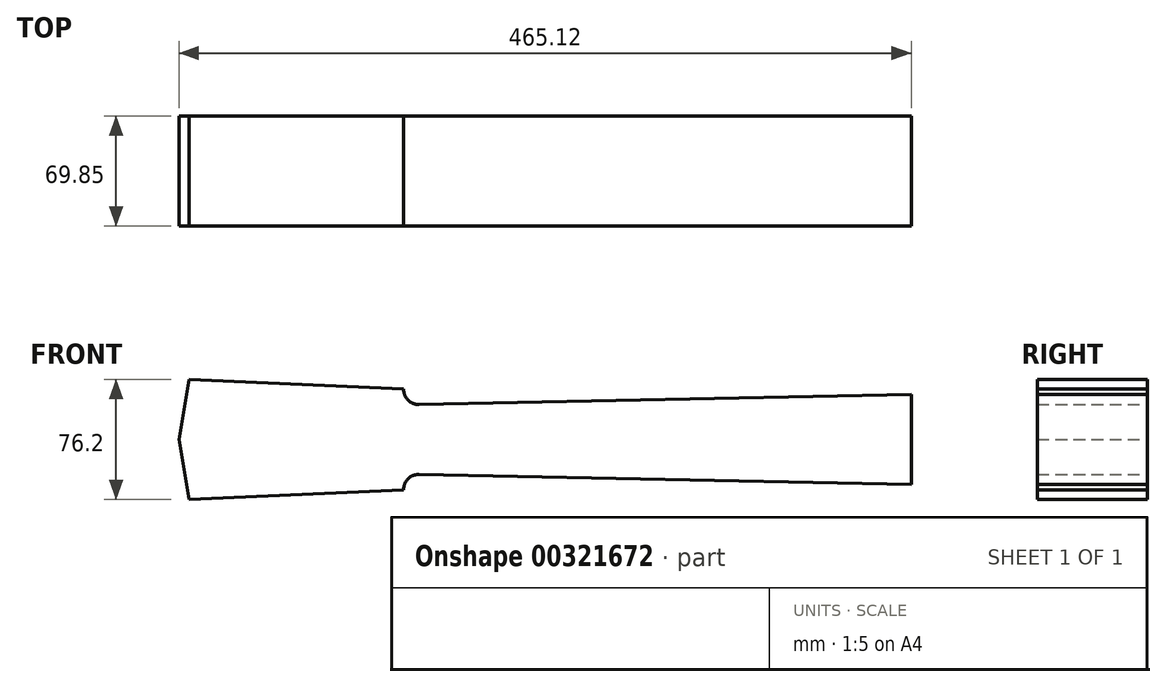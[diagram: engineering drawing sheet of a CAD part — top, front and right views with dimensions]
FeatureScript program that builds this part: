
annotation { "Feature Type Name" : "Feature", "Feature Type Description" : "" }
export const myFeature = defineFeature(function(context is Context, id is Id, definition is map)
    precondition{}
    {
        {
            var Q0;
            Q0=qCreatedBy(makeId("Front.planeOp"),FACE);
            var sketch = newSketch(context, id + "F0", { "sketchPlane" : qUnion([Q0])});
            skLineSegment(sketch, "E0", {"start": v(0, -28.57) * mm, "end": v(0, 28.57) * mm});
            skLineSegment(sketch, "E1", {"start": v(0, 28.58) * mm, "end": v(-312.72, 22.22) * mm});
            skLineSegment(sketch, "E2", {"start": v(-322.44, 32.16) * mm, "end": v(-458.77, 38.1) * mm});
            skLineSegment(sketch, "E3", {"start": v(-458.77, 38.1) * mm, "end": v(-465.12, 0) * mm});
            skLineSegment(sketch, "E4", {"start": v(-465.12, 0) * mm, "end": v(-458.77, -38.1) * mm});
            skLineSegment(sketch, "E5", {"start": v(-458.77, -38.1) * mm, "end": v(-322.44, -32.17) * mm});
            skLineSegment(sketch, "E6", {"start": v(-312.72, -22.23) * mm, "end": v(0, -28.58) * mm});
            skArc(sketch, "E7", {"start": v(-322.44, 32.16) * mm, "mid": v(-319.73, 25.1) * mm, "end": v(-312.72, 22.23) * mm});
            skArc(sketch, "E8", {"start": v(-312.72, -22.23) * mm, "mid": v(-319.74, -25.1) * mm, "end": v(-322.44, -32.17) * mm});
            skPoint(sketch, "E9.orphan", {"position": v(-312.72, -31.75) * mm});
            skSolve(sketch);
        }
        {
            var Q0;
            Q0=makeQuery(id+"F0.imprint","IMPRINT",FACE,{"disambiguationData":[TD([[makeQuery(id+"F0.imprint","IMPRINT",EDGE,{"derivedFrom":sQuery(id+"F0.wireOp",EDGE,"E0")}),1.0]])]});
            extrude(context, id + "F1", {"entities" : qUnion([Q0]), "depth" : 69.85 * mm});
        }
    });
